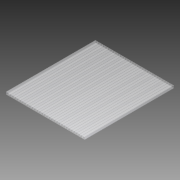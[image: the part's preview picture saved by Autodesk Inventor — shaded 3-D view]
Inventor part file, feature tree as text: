
AUTODESK INVENTOR PART (.ipt)
format: ipt  version: 2012 (Build 160160000, 160)  size: 216,576 bytes
history: native  units: in
note: dims shown in document units (in); Inventor stores cm internally (conversion verified against a paired STEP export)
features: extrude x1, sketch x1
ambient origin geometry x8: Origin, YZ Plane, XZ Plane, XY Plane, X Axis, Y Axis, Z Axis, Center Point
bodies: Solid1 (feature_tree)
feature tree (2):
  extrude  "Extrusion1"  Depth=0.25in
  sketch  "Sketch1"  dims[d0=8.02in d1=0.25in d2=0.0201in d3=0.02in d4=0.02in d5=0.23in d6=12.5984in d8=0.25in d9=0.3937in d11=1.0in d13=9.125in d14=0.0in]
